# Revit family: SH-2507
name_source: partatom
category: Lighting Fixtures
revit_build: Autodesk Revit 2017 (Build: 20160225_1515(x64)
units: mm (PartAtom-declared; Revit-internal decimal feet)

## family parameters
Always vertical = No
Cut with Voids When Loaded = No
Light Source = No
OmniClass Number = 23.80.70.00
OmniClass Title = Lighting
Part Type = Normal
Room Calculation Point = No
Round Connector Dimension = Use Diameter
Shared = Yes
Work Plane-Based = Yes

## types (4) — shared parameters
Body Material = Aluminum
Default Elevation = 121.9 cm
Diameter = 9.8 cm
Diffuser = Glass.
Flicker = Free Flicker
Height = 18.3 cm
IP = IP65
Lamp = GU10
Manufacturer = SHOA
Model = SH-2507
Protection Class = Class I
Type medule = SMD
URL = https://www.shoaco.com
Voltage/Frequency = 230V/50HZ
Website = www.shoaco.com
color rendering index(CRI) = 80<
consumption current = 0 A
wattage = 7 W

## per-type parameters (varying)
| type | 3000K | 6500K | Body color | color temperature |
| Sh-2507(Black color-3000K-Gu10) | Yes | No | Black color | 3000K |
| Sh-2507(Black color-6500K-GU10) | No | Yes | Black color | 6500K |
| Sh-2507(White color-3000K-Gu10) | Yes | No | White color | 3000K |
| Sh-2507(White color-6500K-GU10) | No | Yes | White color | 6500K |

## geometry (parser evidence)
native form markers: Sweep x9
no freeform markers — native parametric forms only
